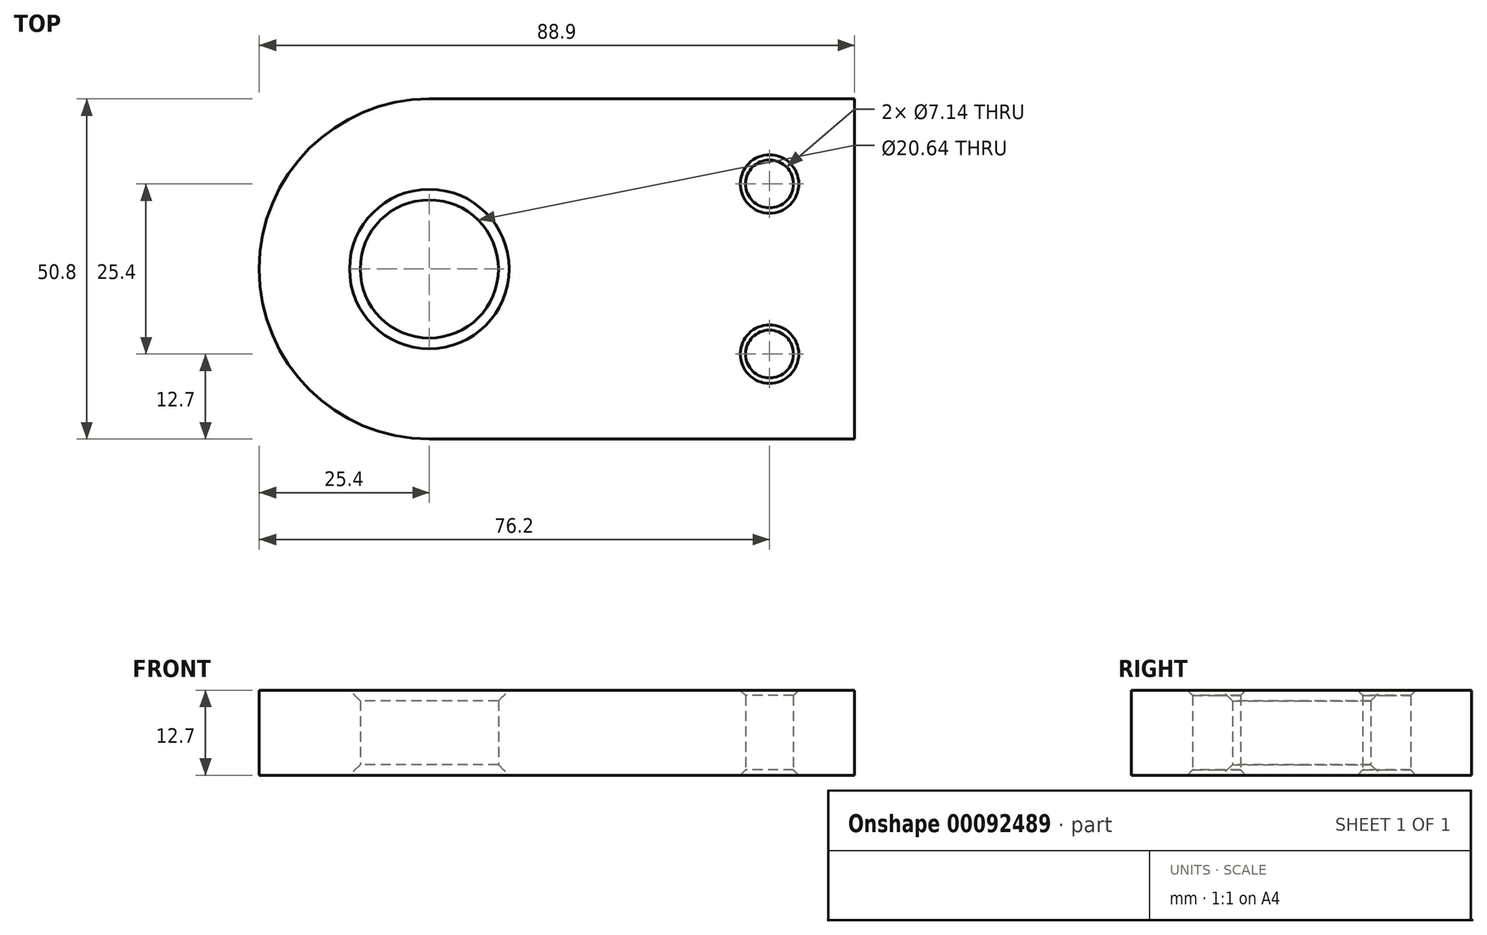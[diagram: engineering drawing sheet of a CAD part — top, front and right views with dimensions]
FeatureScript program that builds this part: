
annotation { "Feature Type Name" : "Feature", "Feature Type Description" : "" }
export const myFeature = defineFeature(function(context is Context, id is Id, definition is map)
    precondition{}
    {
        {
            var Q0;
            Q0=qCreatedBy(makeId("Top.planeOp"),FACE);
            var sketch = newSketch(context, id + "F0", { "sketchPlane" : qUnion([Q0])});
            skCircle(sketch, "E0", {"center": v(0, 0) * mm, "radius": 25.4 * mm});
            skLineSegment(sketch, "E1.bottom", {"start": v(0, -25.4) * mm, "end": v(63.5, -25.4) * mm});
            skLineSegment(sketch, "E1.top", {"start": v(0, 25.4) * mm, "end": v(63.5, 25.4) * mm});
            skLineSegment(sketch, "E1.left", {"start": v(0, -25.4) * mm, "end": v(0, 25.4) * mm});
            skLineSegment(sketch, "E1.right", {"start": v(63.5, -25.4) * mm, "end": v(63.5, 25.4) * mm});
            skCircle(sketch, "E2", {"center": v(0, 0) * mm, "radius": 10.32 * mm});
            skLineSegment(sketch, "E3", {"start": v(0, 0) * mm, "end": v(50.8, 0) * mm, "construction": true});
            skPoint(sketch, "E3.endSnap0", {"position": v(63.5, 0) * mm});
            skLineSegment(sketch, "E4", {"start": v(50.8, 0) * mm, "end": v(50.8, 12.7) * mm, "construction": true});
            skLineSegment(sketch, "E5", {"start": v(50.8, 0) * mm, "end": v(50.8, -12.7) * mm, "construction": true});
            skCircle(sketch, "E6", {"center": v(50.8, -12.7) * mm, "radius": 3.57 * mm});
            skCircle(sketch, "E7", {"center": v(50.8, 12.7) * mm, "radius": 3.57 * mm});
            skSolve(sketch);
        }
        {
            var Q0;
            {var subQ0=sQuery(id+"F0.wireOp",EDGE,"E1.left");Q0=makeQuery(id+"F0.imprint","IMPRINT",FACE,{"disambiguationData":[TD([[makeQuery(id+"F0.imprint","IMPRINT",EDGE,{"derivedFrom":subQ0}),1.0]])]});}
            var Q1;
            {var subQ1=sQuery(id+"F0.wireOp",EDGE,"E1.bottom");Q1=makeQuery(id+"F0.imprint","IMPRINT",FACE,{"disambiguationData":[TD([[makeQuery(id+"F0.imprint","IMPRINT",EDGE,{"derivedFrom":subQ1}),1.0]])]});}
            var Q2;
            {var subQ0=sQuery(id+"F0.wireOp",EDGE,"E1.left");Q2=makeQuery(id+"F0.imprint","IMPRINT",FACE,{"disambiguationData":[TD([[makeQuery(id+"F0.imprint","IMPRINT",EDGE,{"derivedFrom":subQ0}),-1.0]])]});}
            extrude(context, id + "F1", {"entities" : qUnion([Q0, Q1, Q2]), "depth" : 12.7 * mm});
        }
        {
            var Q0;
            Q0=makeQuery(id+"F1.opExtrude","CAP_EDGE",EDGE,{"disambiguationData":[OSD([sQuery(id+"F0.wireOp",EDGE,"E2")])],"isStart":true});
            var Q1;
            Q1=makeQuery(id+"F1.opExtrude","CAP_EDGE",EDGE,{"disambiguationData":[OSD([sQuery(id+"F0.wireOp",EDGE,"E2")])],"isStart":false});
            chamfer(context, id + "F2", {"entities" : qUnion([Q0, Q1]), "width" : 1.59 * mm, "tangentPropagation" : true});
        }
        {
            var Q0;
            Q0=makeQuery(id+"F1.opExtrude","CAP_EDGE",EDGE,{"disambiguationData":[OSD([sQuery(id+"F0.wireOp",EDGE,"E6")])],"isStart":true});
            var Q1;
            Q1=makeQuery(id+"F1.opExtrude","CAP_EDGE",EDGE,{"disambiguationData":[OSD([sQuery(id+"F0.wireOp",EDGE,"E7")])],"isStart":true});
            var Q2;
            Q2=makeQuery(id+"F1.opExtrude","CAP_EDGE",EDGE,{"disambiguationData":[OSD([sQuery(id+"F0.wireOp",EDGE,"E6")])],"isStart":false});
            var Q3;
            Q3=makeQuery(id+"F1.opExtrude","CAP_EDGE",EDGE,{"disambiguationData":[OSD([sQuery(id+"F0.wireOp",EDGE,"E7")])],"isStart":false});
            chamfer(context, id + "F3", {"entities" : qUnion([Q0, Q1, Q2, Q3]), "width" : 0.8 * mm, "tangentPropagation" : true});
        }
    });
